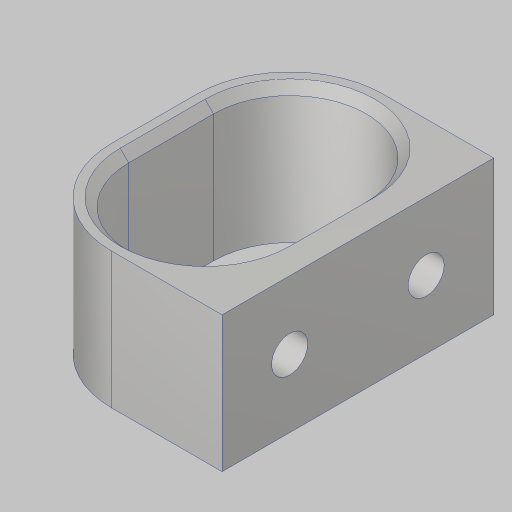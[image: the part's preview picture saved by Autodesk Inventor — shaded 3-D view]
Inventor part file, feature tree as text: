
AUTODESK INVENTOR PART (.ipt)
format: ipt  version: 2023.5 (Build 275446000, 446)  size: 188,416 bytes
history: native  units: in
note: dims shown in document units (in); Inventor stores cm internally (conversion verified against a paired STEP export)
features: projected_geometry x5, extrude x4, sketch x3, chamfer x1, thicken_offset x1
ambient origin geometry x8: Origin, YZ Plane, XZ Plane, XY Plane, X Axis, Y Axis, Z Axis, Center Point
bodies: Solid1 (feature_tree)
feature tree (14):
  sketch  "Sketch1"  dims[d1=1.375in d2=0.125in]
  extrude  "Extrusion1"  Depth=1.375in
  extrude  "Extrusion2"  Depth=1.0in TaperAngle=0.0deg
  extrude  "Extrusion3"  Depth=1.0in
  chamfer  "Chamfer1"  Distance=1.0in
  extrude  "Extrusion4"  Depth=1.0in TaperAngle=0.0deg
  thicken_offset  "Thicken1"
  sketch  "Sketch2"  dims[d3=2.0in d4=1.0in d5=0.0in]
  projected_geometry  "Projected Loop1"
  projected_geometry  "Projected Loop2"
  projected_geometry  "Projected Loop3"
  sketch  "Sketch3"  dims[d6=0.2657in d7=1.005in d8=1.0in d9=0.0in d10=1.0in d11=0.0in d12=0.0625in d13=0.125in d14=45.0deg d15=0.25in d16=0.0in d17=0.125in d18=0.125in]
  projected_geometry  "Projected Loop4"
  projected_geometry  "Projected Loop5"
